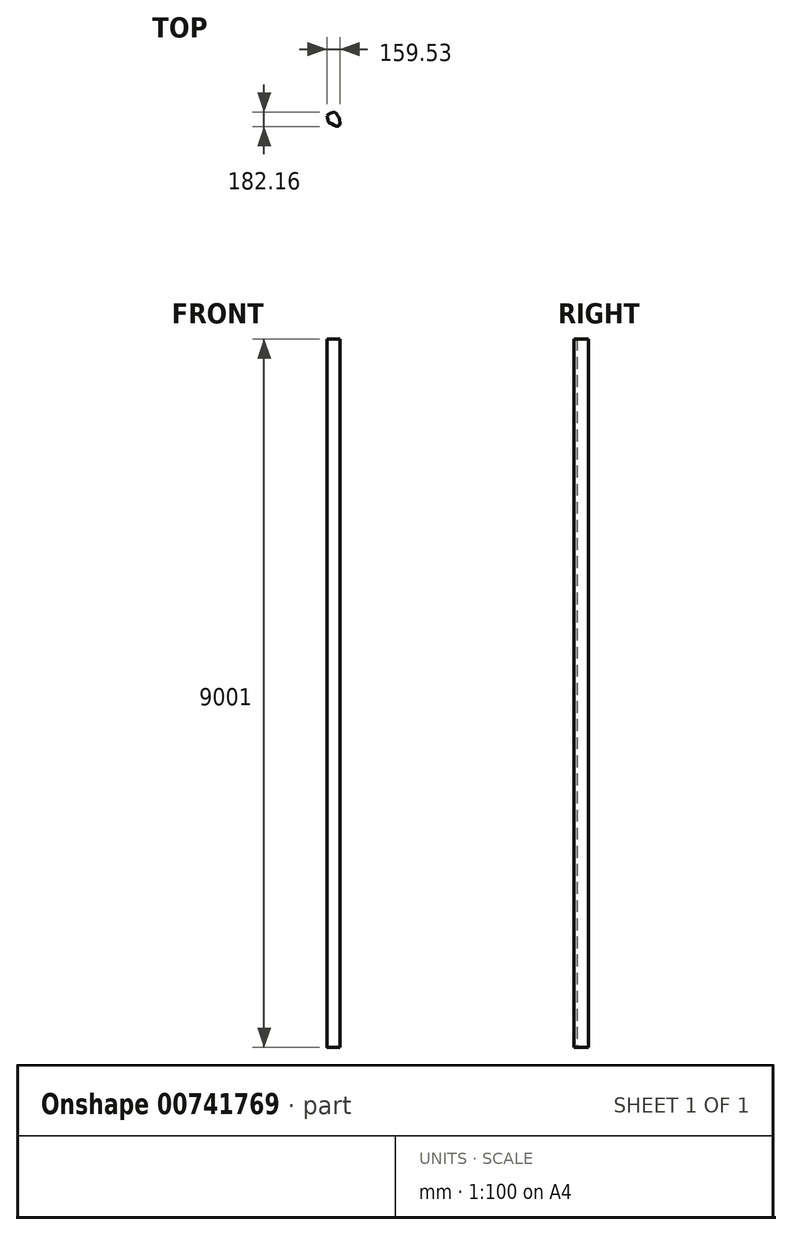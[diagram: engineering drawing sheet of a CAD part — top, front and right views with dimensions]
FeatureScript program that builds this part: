
annotation { "Feature Type Name" : "Feature", "Feature Type Description" : "" }
export const myFeature = defineFeature(function(context is Context, id is Id, definition is map)
    precondition{}
    {
        {
            var Q0;
            Q0=qCreatedBy(makeId("Top.planeOp"),FACE);
            var sketch = newSketch(context, id + "F0", { "sketchPlane" : qUnion([Q0])});
            skLineSegment(sketch, "E0", {"start": v(-105.99, -7.93) * mm, "end": v(-12.23, -7.93) * mm});
            skLineSegment(sketch, "E1", {"start": v(-12.23, -7.93) * mm, "end": v(-18.86, -54.47) * mm});
            skLineSegment(sketch, "E2", {"start": v(-18.86, -54.47) * mm, "end": v(-84.72, -45.08) * mm});
            skLineSegment(sketch, "E3", {"start": v(-84.72, -45.08) * mm, "end": v(-105.99, -7.93) * mm});
            skSolve(sketch);
        }
        {
            var Q0;
            Q0=makeQuery(id+"F0.imprint","IMPRINT",FACE,{"disambiguationData":[TD([[makeQuery(id+"F0.imprint","IMPRINT",EDGE,{"derivedFrom":sQuery(id+"F0.wireOp",EDGE,"E0")}),-1.0]])]});
            extrude(context, id + "F1", {"entities" : qUnion([Q0]), "depth" : 105 * mm, "offsetDistance" : 25.4 * mm});
        }
        {
            var Q0;
            Q0=qCreatedBy(makeId("Top.planeOp"),FACE);
            var sketch = newSketch(context, id + "F2", { "sketchPlane" : qUnion([Q0])});
            skFitSpline(sketch, "E4", {"points": [v(-130.23, 42.67) * mm, v(-104.13, -54.95) * mm, v(-84.33, -56.45) * mm, v(14.73, -92.14) * mm, v(18.46, 21.63) * mm, v(10.34, 27.05) * mm, v(-32.82, 84.7) * mm, v(-107.98, 59.66) * mm, v(-130.23, 42.67) * mm]});
            skSolve(sketch);
        }
        {
            var Q0;
            Q0=makeQuery(id+"F2.imprint","IMPRINT",FACE,{"disambiguationData":[TD([[makeQuery(id+"F2.imprint","IMPRINT",EDGE,{"derivedFrom":sQuery(id+"F2.wireOp",EDGE,"E4")}),1.0]])]});
            extrude(context, id + "F3", {"entities" : qUnion([Q0]), "operationType" : NewBodyOperationType.ADD, "depth" : 9001 * mm, "offsetDistance" : 25.4 * mm});
        }
    });
